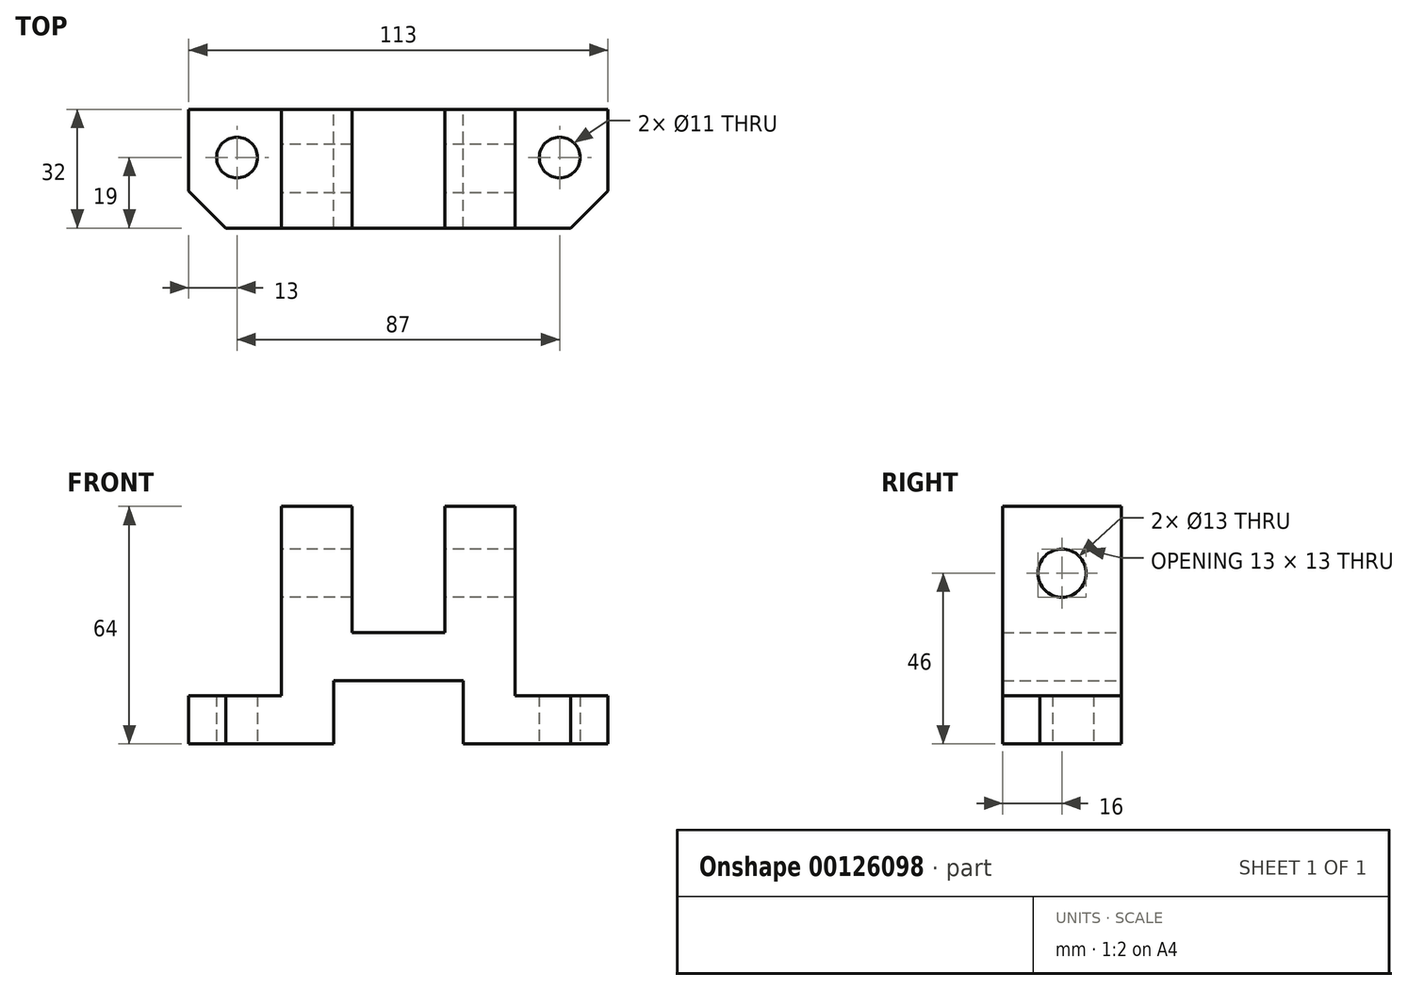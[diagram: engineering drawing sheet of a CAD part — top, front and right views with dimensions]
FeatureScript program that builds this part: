
annotation { "Feature Type Name" : "Feature", "Feature Type Description" : "" }
export const myFeature = defineFeature(function(context is Context, id is Id, definition is map)
    precondition{}
    {
        {
            var Q0;
            Q0=qCreatedBy(makeId("Front.planeOp"),FACE);
            var sketch = newSketch(context, id + "F0", { "sketchPlane" : qUnion([Q0])});
            skLineSegment(sketch, "E0", {"start": v(0, 0) * mm, "end": v(0, 13) * mm});
            skLineSegment(sketch, "E1", {"start": v(0, 13) * mm, "end": v(25, 13) * mm});
            skLineSegment(sketch, "E2", {"start": v(25, 13) * mm, "end": v(25, 64) * mm});
            skLineSegment(sketch, "E3", {"start": v(25, 64) * mm, "end": v(44, 64) * mm});
            skLineSegment(sketch, "E4", {"start": v(44, 64) * mm, "end": v(44, 30) * mm});
            skLineSegment(sketch, "E5", {"start": v(44, 30) * mm, "end": v(69, 30) * mm});
            skLineSegment(sketch, "E6", {"start": v(69, 30) * mm, "end": v(69, 64) * mm});
            skLineSegment(sketch, "E7", {"start": v(69, 64) * mm, "end": v(88, 64) * mm});
            skLineSegment(sketch, "E8", {"start": v(88, 64) * mm, "end": v(88, 13) * mm});
            skLineSegment(sketch, "E9", {"start": v(88, 13) * mm, "end": v(113, 13) * mm});
            skLineSegment(sketch, "E10", {"start": v(113, 13) * mm, "end": v(113, 0) * mm});
            skLineSegment(sketch, "E11", {"start": v(113, 0) * mm, "end": v(74, 0) * mm});
            skLineSegment(sketch, "E12", {"start": v(74, 0) * mm, "end": v(74, 17) * mm});
            skLineSegment(sketch, "E13", {"start": v(74, 17) * mm, "end": v(39, 17) * mm});
            skLineSegment(sketch, "E14", {"start": v(39, 17) * mm, "end": v(39, 0) * mm});
            skLineSegment(sketch, "E15", {"start": v(39, 0) * mm, "end": v(0, 0) * mm});
            skSolve(sketch);
        }
        {
            var Q0;
            Q0=makeQuery(id+"F0.imprint","IMPRINT",FACE,{"disambiguationData":[TD([[makeQuery(id+"F0.imprint","IMPRINT",EDGE,{"derivedFrom":sQuery(id+"F0.wireOp",EDGE,"E0")}),-1.0]])]});
            extrude(context, id + "F1", {"entities" : qUnion([Q0]), "depth" : 32 * mm});
        }
        {
            var Q0;
            Q0=qCreatedBy(makeId("Right.planeOp"),FACE);
            var sketch = newSketch(context, id + "F2", { "sketchPlane" : qUnion([Q0])});
            skLineSegment(sketch, "E16", {"start": v(0, 0) * mm, "end": v(0, 64) * mm});
            skLineSegment(sketch, "E17", {"start": v(0, 64) * mm, "end": v(-32, 64) * mm});
            skLineSegment(sketch, "E18", {"start": v(-32, 64) * mm, "end": v(-32, 0) * mm});
            skLineSegment(sketch, "E19", {"start": v(-32, 0) * mm, "end": v(0, 0) * mm});
            skArc(sketch, "E20", {"start": v(0, 60.13) * mm, "mid": v(-16, 64) * mm, "end": v(-32, 60.13) * mm});
            skLineSegment(sketch, "E21", {"start": v(-32, 60.13) * mm, "end": v(-32, 64) * mm});
            skLineSegment(sketch, "E22", {"start": v(0, 60.13) * mm, "end": v(0, 64) * mm});
            skLineSegment(sketch, "E23", {"start": v(-16, 0) * mm, "end": v(-16, 64) * mm, "construction": true});
            skCircle(sketch, "E24", {"center": v(-16, 46) * mm, "radius": 6.5 * mm});
            skSolve(sketch);
        }
        {
            var Q0;
            Q0=makeQuery(id+"F2.imprint","IMPRINT",FACE,{"disambiguationData":[TD([[makeQuery(id+"F2.imprint","IMPRINT",EDGE,{"derivedFrom":sQuery(id+"F2.wireOp",EDGE,"E24")}),1.0]])]});
            var Q1;
            Q1=sQuery(id+"F2.wireOp",EDGE,"E24");
            extrude(context, id + "F3", {"entities" : qUnion([Q0]), "operationType" : NewBodyOperationType.REMOVE, "surfaceEntities" : qUnion([Q1]), "endBound" : BoundingType.THROUGH_ALL, "depth" : 113.67 * mm});
        }
        {
            var Q0;
            Q0=qCreatedBy(makeId("Top.planeOp"),FACE);
            var sketch = newSketch(context, id + "F4", { "sketchPlane" : qUnion([Q0])});
            skLineSegment(sketch, "E25", {"start": v(0, 0) * mm, "end": v(0, -22) * mm});
            skLineSegment(sketch, "E26", {"start": v(0, -22) * mm, "end": v(10, -32) * mm});
            skLineSegment(sketch, "E27", {"start": v(10, -32) * mm, "end": v(103, -32) * mm});
            skLineSegment(sketch, "E28", {"start": v(103, -32) * mm, "end": v(113, -22) * mm});
            skLineSegment(sketch, "E29", {"start": v(113, -22) * mm, "end": v(113, 0) * mm});
            skLineSegment(sketch, "E30", {"start": v(113, 0) * mm, "end": v(0, 0) * mm});
            skLineSegment(sketch, "E31", {"start": v(0, -22) * mm, "end": v(0, -32) * mm});
            skLineSegment(sketch, "E32", {"start": v(0, -32) * mm, "end": v(10, -32) * mm});
            skLineSegment(sketch, "E33", {"start": v(103, -32) * mm, "end": v(113, -32) * mm});
            skLineSegment(sketch, "E34", {"start": v(113, -32) * mm, "end": v(113, -22) * mm});
            skCircle(sketch, "E35", {"center": v(13, -13) * mm, "radius": 5.5 * mm});
            skCircle(sketch, "E36", {"center": v(100, -13) * mm, "radius": 5.5 * mm});
            skSolve(sketch);
        }
        {
            var Q0;
            Q0=makeQuery(id+"F4.imprint","IMPRINT",FACE,{"disambiguationData":[TD([[makeQuery(id+"F4.imprint","IMPRINT",EDGE,{"derivedFrom":sQuery(id+"F4.wireOp",EDGE,"E26")}),-1.0]])]});
            var Q1;
            Q1=sQuery(id+"F4.wireOp",EDGE,"E26");
            var Q2;
            Q2=sQuery(id+"F4.wireOp",EDGE,"E32");
            var Q3;
            Q3=sQuery(id+"F4.wireOp",EDGE,"E31");
            extrude(context, id + "F5", {"entities" : qUnion([Q0]), "operationType" : NewBodyOperationType.REMOVE, "surfaceEntities" : qUnion([Q1, Q2, Q3]), "endBound" : BoundingType.THROUGH_ALL, "depth" : 25 * mm});
        }
        {
            var Q0;
            Q0=makeQuery(id+"F4.imprint","IMPRINT",FACE,{"disambiguationData":[TD([[makeQuery(id+"F4.imprint","IMPRINT",EDGE,{"derivedFrom":sQuery(id+"F4.wireOp",EDGE,"E28")}),-1.0]])]});
            var Q1;
            Q1=sQuery(id+"F4.wireOp",EDGE,"E34");
            var Q2;
            Q2=sQuery(id+"F4.wireOp",EDGE,"E28");
            var Q3;
            Q3=sQuery(id+"F4.wireOp",EDGE,"E33");
            extrude(context, id + "F6", {"entities" : qUnion([Q0]), "operationType" : NewBodyOperationType.REMOVE, "surfaceEntities" : qUnion([Q1, Q2, Q3]), "endBound" : BoundingType.THROUGH_ALL, "depth" : 25 * mm});
        }
        {
            var Q0;
            Q0=makeQuery(id+"F4.imprint","IMPRINT",FACE,{"disambiguationData":[TD([[makeQuery(id+"F4.imprint","IMPRINT",EDGE,{"derivedFrom":sQuery(id+"F4.wireOp",EDGE,"E35")}),1.0]])]});
            var Q1;
            Q1=sQuery(id+"F4.wireOp",EDGE,"E35");
            extrude(context, id + "F7", {"entities" : qUnion([Q0]), "operationType" : NewBodyOperationType.REMOVE, "surfaceEntities" : qUnion([Q1]), "endBound" : BoundingType.THROUGH_ALL, "depth" : 25 * mm});
        }
        {
            var Q0;
            Q0=makeQuery(id+"F4.imprint","IMPRINT",FACE,{"disambiguationData":[TD([[makeQuery(id+"F4.imprint","IMPRINT",EDGE,{"derivedFrom":sQuery(id+"F4.wireOp",EDGE,"E36")}),1.0]])]});
            var Q1;
            Q1=sQuery(id+"F4.wireOp",EDGE,"E36");
            extrude(context, id + "F8", {"entities" : qUnion([Q0]), "operationType" : NewBodyOperationType.REMOVE, "surfaceEntities" : qUnion([Q1]), "endBound" : BoundingType.THROUGH_ALL, "depth" : 25 * mm});
        }
    });
